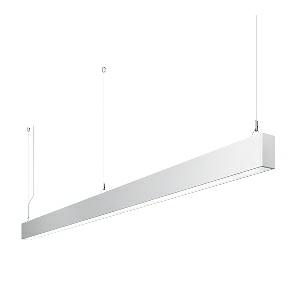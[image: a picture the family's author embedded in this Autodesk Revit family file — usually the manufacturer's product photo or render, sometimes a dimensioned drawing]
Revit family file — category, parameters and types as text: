
# Revit family: dotoo_line_-_dlp_3000_830_d_00805809_5567
name_source: partatom
category: Lighting Fixtures
units: mm (PartAtom-declared; Revit-internal decimal feet)

## family parameters
Cut with Voids When Loaded = No
Host = Face
Light Source = No
Part Type = Normal
Room Calculation Point = No
Round Connector Dimension = Use Diameter
Shared = No

## types (1)
- DOTOO.line - DLP 3000/830/D (1 x LED, 2650 lm, 3000K)
    Apparent Load = 26 VA
    Approval mark = CE
    CIE Flux Codes = 67 91 98 100 100
    Color Rendering = 80-89
    Color Temperature = 3000K
    Control Gear = Electronic ballast
    Default Elevation = 1800 mm
    Description = DLP 3000/830/D|Suspended luminaire|light source: LED|connected load: 220-240V, 50/60Hz|Power consumption: approx. 26 W|standby: approx. 0,15|luminous flux: 2650 lm|luminous efficacy: 101 lm/W|light distribution: Direct|direct ratio: approx. 100 %|colour temperature: Warm white, ca. 3000 K|color rendering index (CRI): >= 80|chromaticity tolerance:  3 SDCM|System of protection: IP 40|technology: Continuously dimmable|luminaire body|material: Sectional aluminium|colour: White|lamp cover: Acrylic (PMMA), Clear|mains lead: 2.00 m With free stranded wires|Fastening: Steel cable 0.3 - 0.7 m|glare control: Prism aperture|luminance(L65): <= 3000 cd/m|unified glare rating(4H 8H): <=  19|special features: DALI Load 1x, TouchDIM - dimming via standard switch, Flicker-free, Suitable as emergency lighting|
    Frequency = 50 Hz
    Height = 110 mm
    Lamp = 1 x LED
    Lamp Light Flux = 2650 lm
    Lamp count = 1
    Length = 2256 mm
    Luminous efficacy = 102 lm/W
    Manufacturer = Waldmann
    ModVariant = No
    Model = 00805809
    Mounting Place = Ceiling
    Mounting Type = Pendant
    Number of Poles = 1
    OnlyDefault = Yes
    Power Factor = 1
    Product Name = DOTOO.line - DLP 3000/830/D
    Product group = Suspended luminaire
    ProductGroupID = 9
    Protection Class = Protection class I
    Protection Degree = IP 40
    RLX_Detail_Level = 1
    RLX_Emergency_Light_Flux = 0 lm
    RLX_Emergency_Type = 0
    RLX_Emergency_Type_DB = No
    RlxData = <blob elided: 21329 chars, md5=8085dac5>
    Socket = socket
    Standby Power = 0 W
    System Light Flux = 2650 lm
    System Power = 26 W
    Type Comments = Product without accessories
    Type Image = 113293000-00692530.jpg
    URL = http://relux.com
    VarID = ---
    Voltage = 230 V
    Voltage Range = 220-240 V
    Weight = 0.00 kg
    Width = 60 mm  [stored 0.19685 ft]

note: [stored X ft] marks values corroborated as IEEE doubles in the binary element streams (Revit-internal decimal feet)

## geometry (parser evidence)
native form markers: Blend x4, Sweep x10
no freeform markers — native parametric forms only
